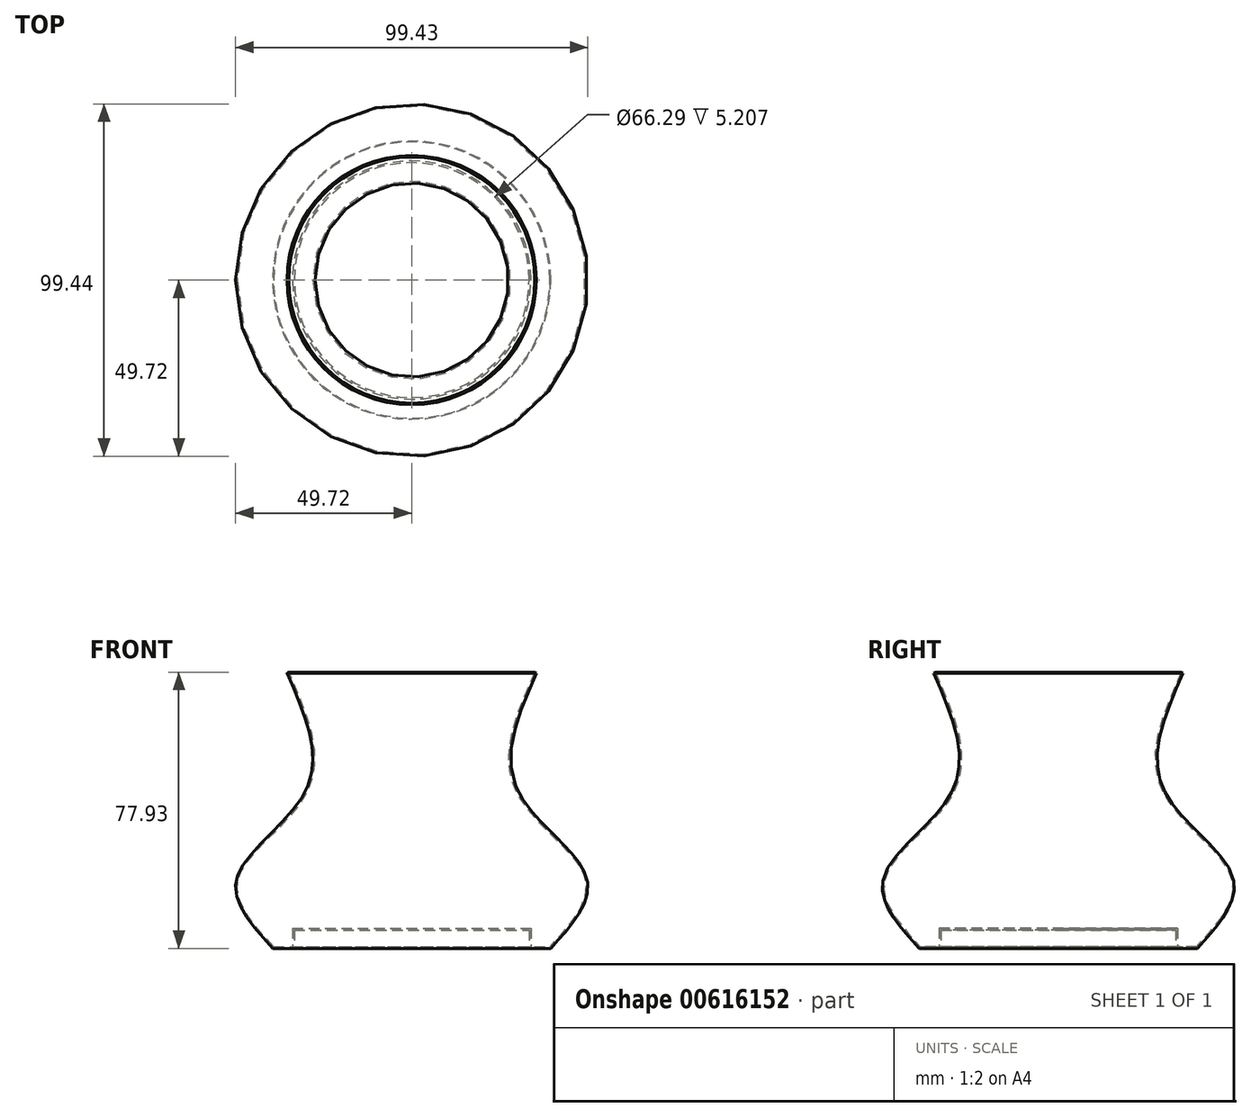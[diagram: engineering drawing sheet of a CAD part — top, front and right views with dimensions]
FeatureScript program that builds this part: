
annotation { "Feature Type Name" : "Feature", "Feature Type Description" : "" }
export const myFeature = defineFeature(function(context is Context, id is Id, definition is map)
    precondition{}
    {
        {
            var Q0;
            Q0=qCreatedBy(makeId("Front.planeOp"),FACE);
            var sketch = newSketch(context, id + "F0", { "sketchPlane" : qUnion([Q0])});
            skLineSegment(sketch, "E0", {"start": v(0, 0) * mm, "end": v(0, 66.42) * mm, "construction": true});
            skLineSegment(sketch, "E1", {"start": v(0, 0) * mm, "end": v(33.15, 0) * mm});
            skLineSegment(sketch, "E2", {"start": v(33.15, 0) * mm, "end": v(33.15, -5.2) * mm});
            skLineSegment(sketch, "E3", {"start": v(33.15, -5.2) * mm, "end": v(39.24, -5.2) * mm});
            skFitSpline(sketch, "E4", {"points": [v(39.24, -5.2) * mm, v(49.4, 14.6) * mm, v(29.6, 40) * mm, v(35.18, 72.52) * mm], "startDerivative": vector(61.28, 67.83) * mm, "endDerivative": vector(41.84, 96.18) * mm});
            skFitSpline(sketch, "E5.0", {"points": [v(38.87, -4.87) * mm, v(40.14, -3.45) * mm, v(42.69, -0.63) * mm, v(46.03, 3.57) * mm, v(48.04, 7.03) * mm, v(48.97, 9.75) * mm, v(49.28, 11.76) * mm, v(49.18, 13.43) * mm, v(48.85, 14.76) * mm, v(48.36, 16.1) * mm, v(47.44, 17.8) * mm, v(45.45, 20.58) * mm, v(42.17, 24.14) * mm, v(38.41, 27.83) * mm, v(35.46, 30.9) * mm, v(33.37, 33.25) * mm, v(31.47, 35.68) * mm, v(30.13, 37.78) * mm, v(29.24, 39.5) * mm, v(28.5, 41.26) * mm, v(27.84, 43.5) * mm, v(27.44, 46.26) * mm, v(27.37, 50.02) * mm, v(28.05, 54.82) * mm, v(29.77, 60.72) * mm, v(32.1, 66.7) * mm, v(33.84, 70.72) * mm, v(34.71, 72.72) * mm]});
            skLineSegment(sketch, "E6.0", {"start": v(0, 0.5) * mm, "end": v(33.15, 0.5) * mm});
            skLineSegment(sketch, "E7.1", {"start": v(33.66, -4.7) * mm, "end": v(39.02, -4.7) * mm});
            skLineSegment(sketch, "E7.2", {"start": v(33.66, 0.5) * mm, "end": v(33.66, -4.7) * mm});
            skLineSegment(sketch, "E7.3", {"start": v(0, 0.5) * mm, "end": v(33.66, 0.5) * mm});
            skLineSegment(sketch, "E8", {"start": v(0, 0.5) * mm, "end": v(0, 0) * mm});
            skLineSegment(sketch, "E9", {"start": v(34.71, 72.72) * mm, "end": v(35.18, 72.52) * mm});
            skSolve(sketch);
        }
        {
            var Q0;
            Q0 = qSketchRegion(id + "F0", true);
            var Q1;
            Q1=sQuery(id+"F0.wireOp",EDGE,"E0");
            revolve(context, id + "F1", {"entities" : qUnion([Q0]), "axis" : qUnion([Q1]), "revolveType" : RevolveType.FULL});
        }
    });
